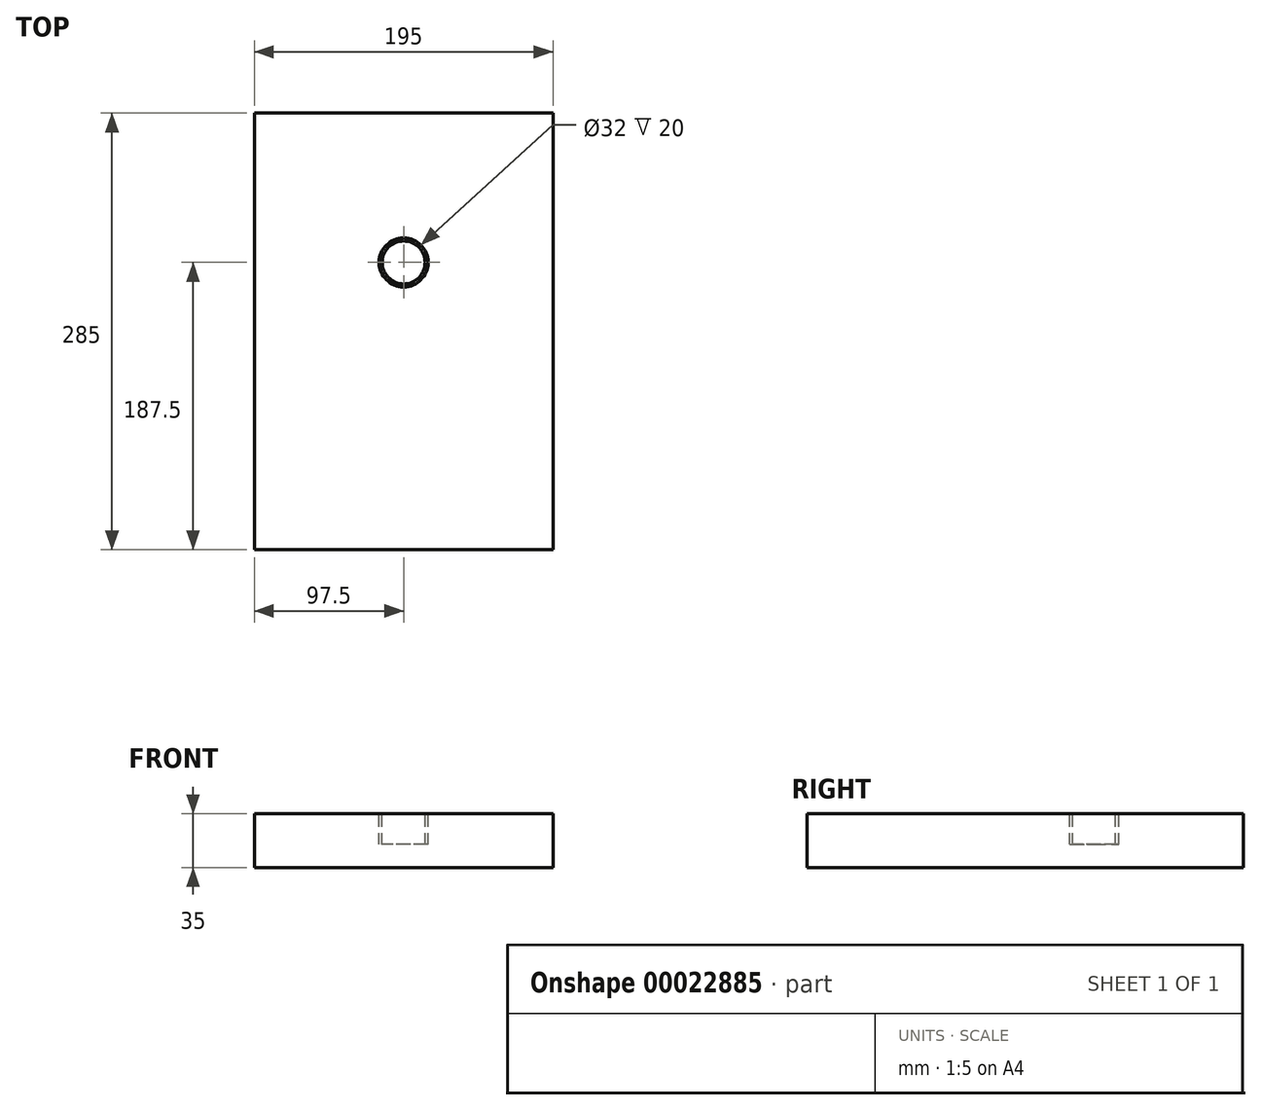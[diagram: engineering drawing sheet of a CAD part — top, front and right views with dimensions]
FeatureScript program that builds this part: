
annotation { "Feature Type Name" : "Feature", "Feature Type Description" : "" }
export const myFeature = defineFeature(function(context is Context, id is Id, definition is map)
    precondition{}
    {
        {
            var Q0;
            Q0=qCreatedBy(makeId("Top.planeOp"),FACE);
            var sketch = newSketch(context, id + "F0", { "sketchPlane" : qUnion([Q0])});
            skLineSegment(sketch, "E0.bottom", {"start": v(-97.5, 97.5) * mm, "end": v(97.5, 97.5) * mm});
            skLineSegment(sketch, "E0.top", {"start": v(-97.5, -187.5) * mm, "end": v(97.5, -187.5) * mm});
            skLineSegment(sketch, "E0.left", {"start": v(-97.5, 97.5) * mm, "end": v(-97.5, -187.5) * mm});
            skLineSegment(sketch, "E0.right", {"start": v(97.5, 97.5) * mm, "end": v(97.5, -187.5) * mm});
            skSolve(sketch);
        }
        {
            var Q0;
            Q0=makeQuery(id+"F0.imprint","IMPRINT",FACE,{"disambiguationData":[TD([[makeQuery(id+"F0.imprint","IMPRINT",EDGE,{"derivedFrom":sQuery(id+"F0.wireOp",EDGE,"E0.bottom")}),-1.0]])]});
            extrude(context, id + "F1", {"entities" : qUnion([Q0]), "depth" : 35 * mm});
        }
        {
            var Q0;
            Q0=makeQuery(id+"F1.opExtrude","CAP_FACE",FACE,{"disambiguationData":[OSD([sQuery(id+"F0.wireOp",EDGE,"E0.bottom"),sQuery(id+"F0.wireOp",EDGE,"E0.top"),sQuery(id+"F0.wireOp",EDGE,"E0.left"),sQuery(id+"F0.wireOp",EDGE,"E0.right")])],"isStart":false});
            var sketch = newSketch(context, id + "F2", { "sketchPlane" : qUnion([Q0])});
            skCircle(sketch, "E1", {"center": v(0, 0) * mm, "radius": 16 * mm});
            skCircle(sketch, "E2", {"center": v(0, 0) * mm, "radius": 14 * mm});
            skSolve(sketch);
        }
        {
            var Q0;
            Q0=makeQuery(id+"F2.imprint","IMPRINT",FACE,{"disambiguationData":[TD([[makeQuery(id+"F2.imprint","IMPRINT",EDGE,{"derivedFrom":sQuery(id+"F2.wireOp",EDGE,"E1")}),1.0]])]});
            extrude(context, id + "F3", {"entities" : qUnion([Q0]), "operationType" : NewBodyOperationType.REMOVE, "oppositeDirection" : true, "depth" : 20 * mm});
        }
    });
